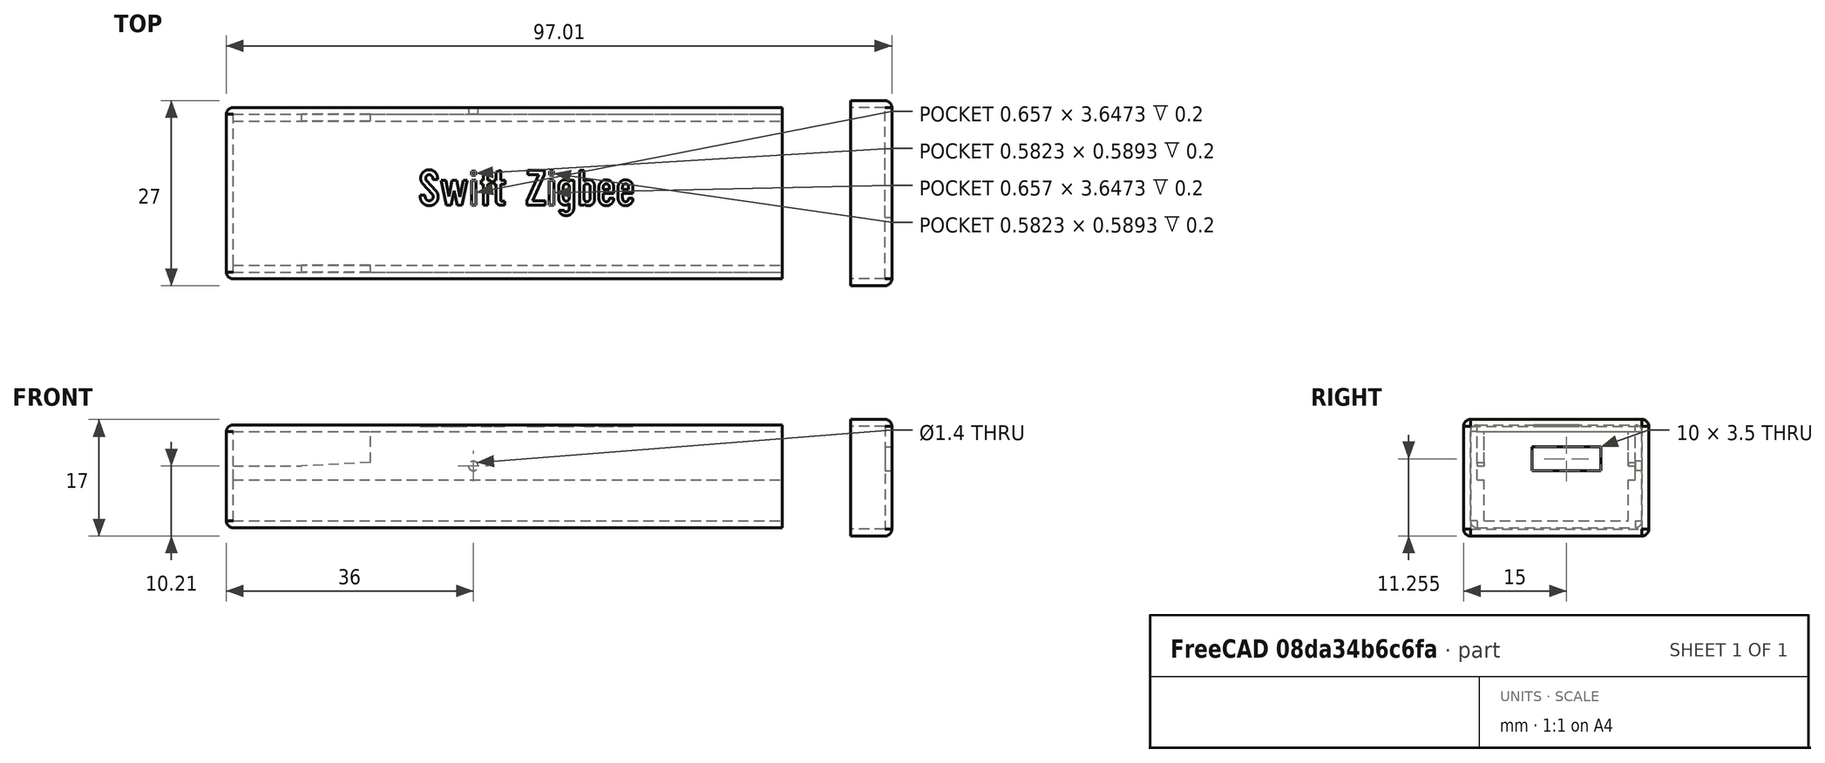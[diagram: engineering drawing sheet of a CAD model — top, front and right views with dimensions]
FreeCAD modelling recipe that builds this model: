
FCSTD DOCUMENT  (FreeCAD 1.0R38641 +468 (Git))
Label: box
License: All rights reserved
LicenseURL: https://en.wikipedia.org/wiki/All_rights_reserved
objects: Part::Box×7, Part::MultiFuse×4, Part::Cut×3, Part::Thickness×2, Part::Chamfer×2, Part::Cylinder×1, Part::Part2DObjectPython×1, Part::Extrusion×1
note: 21 computed .brp shape members not serialized (recipe doc carries the construction recipe); baked Part::Feature solids carry a one-line shape summary decoded from their .brp

FEATURE [Part::Box] Box  label="Cube"
  AttacherType = Attacher::AttachEngine3D
  Height = 13
  Length = 80
  Width = 23
FEATURE [Part::Thickness] Thickness
  Faces = -> Box [Face2]
  Intersection = false
  Join = 0
  Mode = 0
  SelfIntersection = false
  Value = 1
FEATURE [Part::Box] Box001  label="Cube001"
  AttacherType = Attacher::AttachEngine3D
  Height = 6
  Length = 80
  Width = 1
FEATURE [Part::Box] Box002  label="Cube002"
  AttacherType = Attacher::AttachEngine3D
  Height = 6
  Length = 80
  Placement = pos=(0,22,0) rot=(0,0,1;0rad)
  Width = 1
FEATURE [Part::MultiFuse] Fusion
  Shapes = -> [Thickness,Box001]
FEATURE [Part::MultiFuse] Fusion001
  Shapes = -> [Box002,Fusion]
FEATURE [Part::Cylinder] Cylinder  label="Cylindre"
  Angle = 360
  AttacherType = Attacher::AttachEngine3D
  FirstAngle = 0
  Height = 3
  Placement = pos=(35,22,8) rot=(-1,0,0;1.5708rad)
  Radius = 0.7
  SecondAngle = 0
FEATURE [Part::Cut] Cut
  Base = -> Fusion001
  Tool = -> Cylinder
FEATURE [Part::Box] Box003  label="Cube003"
  AttacherType = Attacher::AttachEngine3D
  Height = 5
  Length = 20
  Placement = pos=(0,0,8) rot=(0,0,1;0rad)
  Width = 1
FEATURE [Part::Box] Box004  label="Cube004"
  AttacherType = Attacher::AttachEngine3D
  Height = 5
  Length = 20
  Placement = pos=(0,22,8) rot=(0,0,1;0rad)
  Width = 1
FEATURE [Part::Chamfer] Chamfer
  Base = -> Box003
  EdgeLinks = -> Box003 [Edge8]
  Edges = 1 edges: [Edge8 r1=0.5 r2=10]
FEATURE [Part::Chamfer] Chamfer001
  Base = -> Box004
  EdgeLinks = -> Box004 [Edge8]
  Edges = 1 edges: [Edge8 r1=0.5 r2=10]
FEATURE [Part::Part2DObjectPython] ShapeString  # Draft 2D object (typed FeaturePython)
  FontFile = <userpath>/TrueTypeFonts/gligoth.TTF
  Fuse = false
  Justification = 6
  JustificationReference = 0
  KeepLeftMargin = true
  MakeFace = true
  ObliqueAngle = 0
  Placement = pos=(8,-13,-0.4) rot=(0,0,1;0rad)
  ScaleToSize = false
  Size = 6
  String = Swift Zigbee
  Tracking = 0
FEATURE [Part::Extrusion] Extrude
  Base = -> ShapeString
  Dir = (0,0,1)
  DirMode = 2
  FaceMakerClass = Part::FaceMakerBullseye
  FaceMakerMode = 3
  LengthFwd = 1
  LengthRev = 0
  Placement = pos=(18.9098,22.7483,14.2) rot=(0,0,1;0rad)
  Solid = false
  Symmetric = false
FEATURE [Part::Cut] Cut001
  Base = -> Cut
  Tool = -> Extrude
FEATURE [Part::MultiFuse] Fusion002
  Shapes = -> [Cut001,Chamfer001]
FEATURE [Part::MultiFuse] Fusion003  label="Main"
  Shapes = -> [Fusion002,Chamfer]
FEATURE [Part::Box] Box005  label="Creux"
  AttacherType = Attacher::AttachEngine3D
  Height = 15
  Length = 5
  Placement = pos=(81,0,0) rot=(0,0,1;0rad)
  Width = 25
FEATURE [Part::Thickness] Thickness001  label="Bord"
  Faces = -> Box005 [Face2]
  Intersection = false
  Join = 0
  Mode = 2
  Placement = pos=(173,-1,14) rot=(0,1,0;3.14159rad)
  SelfIntersection = false
  Value = 1
FEATURE [Part::Box] Box006  label="Fente"
  AttacherType = Attacher::AttachEngine3D
  Height = 3.5
  Length = 4
  Placement = pos=(90,8,7.5) rot=(0,0,1;0rad)
  Width = 10
FEATURE [Part::Cut] Cut002  label="Lid"
  Base = -> Thickness001
  Placement = pos=(3.01038,0,-0.205466) rot=(0,0,1;0rad)
  Tool = -> Box006
